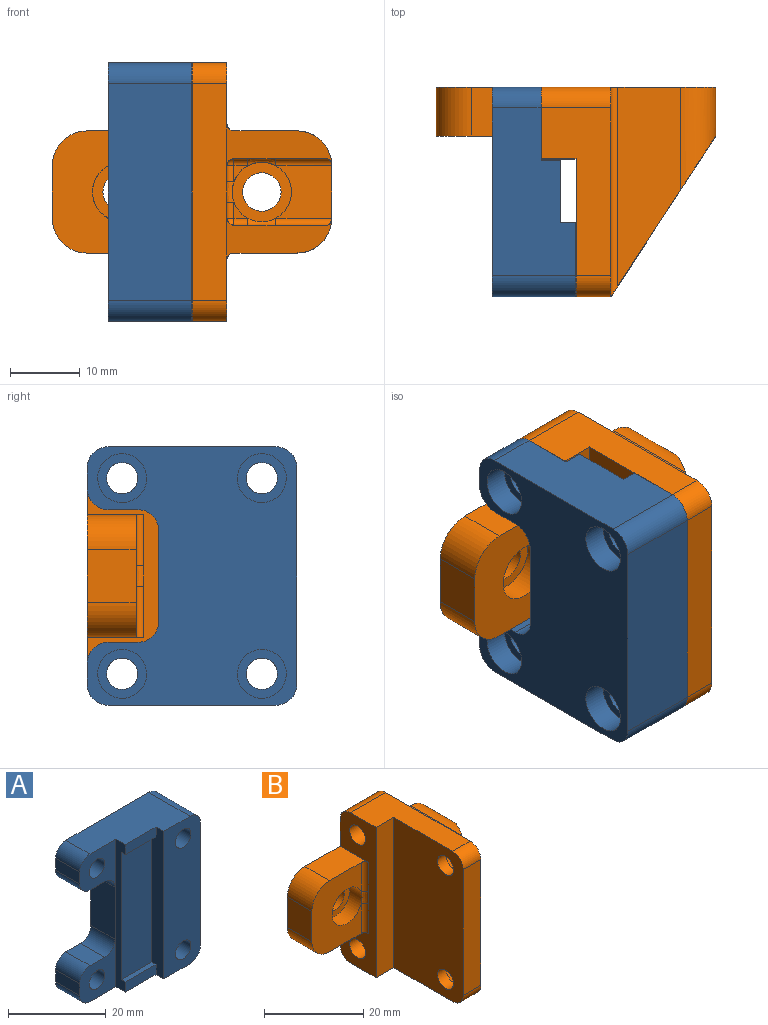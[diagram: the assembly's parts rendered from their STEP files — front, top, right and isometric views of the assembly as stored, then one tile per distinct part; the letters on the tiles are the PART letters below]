
ASSEMBLY  parts=2 mates=1
PART A: 38 faces, bbox 30x12x37 mm
  f0: cylinder r=2.25mm len=4.5mm, axis (0,1,0), area 49.5mm2, adj f6,f31
  f1: cylinder r=2.25mm len=4.5mm, axis (0,1,0), area 49.5mm2, adj f6,f33
  f2: cylinder r=2.25mm len=8.5mm, axis (0,1,0), area 120.2mm2, adj f16,f35
  f3: cylinder r=2.25mm len=8.5mm, axis (0,1,0), area 120.2mm2, adj f16,f37
  f4: plane 37x3.5mm, normal (-1,0,0), area 123.2mm2, adj f5,f8,f14,f16,f18,f19,f20,f21
  f5: plane 32x8.88mm, normal (0,-1,0), area 284mm2, adj f4,f17,f18,f20
  f6: plane 37x10.5mm, normal (0,-1,0), area 158.1mm2, adj f0,f1,f8,f9,f10,f11,f12,f13
  f7: plane 31x12mm, normal (1,0,0), area 372mm2, adj f15,f16,f22,f23
  f8: plane 24x12mm, normal (0,0,1), area 230.5mm2, adj f4,f6,f15,f16,f17,f19,f22,f24
  f9: plane 7x3mm, normal (-1,0,0), area 21mm2, adj f6,f15,f24,f25
  f10: plane 7x4.25mm, normal (0,0,-1), area 29.8mm2, adj f6,f15,f25,f26
  f11: plane 13x7mm, normal (-1,0,0), area 91mm2, adj f6,f15,f26,f27
  f12: plane 7x4.25mm, normal (0,0,1), area 29.8mm2, adj f6,f15,f27,f28
  f13: plane 7x3mm, normal (-1,0,0), area 21mm2, adj f6,f15,f28,f29
  f14: plane 24x12mm, normal (0,0,-1), area 230.5mm2, adj f4,f6,f15,f16,f17,f21,f23,f29
  f15: plane 37x30mm, normal (0,1,0), area 753.6mm2, adj f7,f8,f9,f10,f11,f12,f13,f14
  f16: plane 37x10.63mm, normal (0,-1,0), area 357.5mm2, adj f2,f3,f4,f7,f8,f14,f22,f23
  f17: plane 37x2.75mm, normal (-1,0,0), area 61.7mm2, adj f5,f6,f8,f14,f18,f19,f20,f21
  f18: plane 8.88x1.25mm, normal (0,0,-1), area 11.1mm2, adj f4,f5,f17,f19
  f19: plane 8.88x2.5mm, normal (0,-1,0), area 22.2mm2, adj f4,f8,f17,f18
  f20: plane 8.88x1.25mm, normal (0,0,1), area 11.1mm2, adj f4,f5,f17,f21
  f21: plane 8.88x2.5mm, normal (0,-1,0), area 22.2mm2, adj f4,f14,f17,f20
  f22: cylinder r=3mm len=12mm, axis (0,-1,0), area 56.5mm2, adj f7,f8,f15,f16
  f23: cylinder r=3mm len=12mm, axis (0,1,0), area 56.5mm2, adj f7,f14,f15,f16
  f24: cylinder r=3mm len=7mm, axis (0,1,0), area 33mm2, adj f6,f8,f9,f15
  f25: cylinder r=3mm len=7mm, axis (0,1,0), area 33mm2, adj f6,f9,f10,f15
  f26: cylinder r=3mm len=7mm, axis (0,-1,0), area 33mm2, adj f6,f10,f11,f15
  f27: cylinder r=3mm len=7mm, axis (0,1,0), area 33mm2, adj f6,f11,f12,f15
  f28: cylinder r=3mm len=7mm, axis (0,1,0), area 33mm2, adj f6,f12,f13,f15
  f29: cylinder r=3mm len=7mm, axis (0,1,0), area 33mm2, adj f6,f13,f14,f15
  f30: cylinder r=3.5mm len=7mm, axis (0,1,0), area 77mm2, adj f15,f31
  f31: plane 7x7mm, normal (0,1,0), area 22.6mm2, adj f0,f30
  f32: cylinder r=3.5mm len=7mm, axis (0,1,0), area 77mm2, adj f15,f33
  f33: plane 7x7mm, normal (0,1,0), area 22.6mm2, adj f1,f32
  f34: cylinder r=3.5mm len=7mm, axis (0,1,0), area 77mm2, adj f15,f35
  f35: plane 7x7mm, normal (0,1,0), area 22.6mm2, adj f2,f34
  f36: cylinder r=3.5mm len=7mm, axis (0,1,0), area 77mm2, adj f15,f37
  f37: plane 7x7mm, normal (0,1,0), area 22.6mm2, adj f3,f36
PART B: 88 faces, bbox 40.6x30.6x37.6 mm
  f0: cylinder r=2.25mm len=4.5mm, axis (-1,0,0), area 35.3mm2, adj f28,f81
  f1: cylinder r=2.25mm len=4.5mm, axis (-1,0,0), area 35.3mm2, adj f28,f74
  f2: cylinder r=2.25mm len=7.5mm, axis (-1,0,0), area 106mm2, adj f9,f67
  f3: cylinder r=2.25mm len=7.5mm, axis (-1,0,0), area 106mm2, adj f9,f60
  f4: plane 8x7.5mm, normal (0,-1,0), area 48mm2, adj f16,f24,f40,f52
  f5: plane 2.31x2mm, normal (0,-1,0), area 1.7mm2, adj f24,f47,f50
  f6: plane 30x8.75mm, normal (1,0,0), area 173.8mm2, adj f11,f18,f23,f39,f56,f59,f61,f62
  f7: plane 2.31x2mm, normal (0,-1,0), area 1.7mm2, adj f24,f42,f45
  f8: plane 22.03x7.5mm, normal (1,0,0), area 165mm2, adj f11,f43,f45,f46,f47,f48
  f9: plane 37x10.25mm, normal (-1,0,0), area 203.6mm2, adj f2,f3,f10,f18,f19,f21,f23,f29
  f10: plane 24x10mm, normal (0,0,-1), area 156.2mm2, adj f9,f22,f28,f29,f38,f58
  f11: plane 31x5mm, normal (0,-1,0), area 155mm2, adj f6,f8,f22,f28,f30,f32,f38,f39
  f12: plane 17.5x14mm, normal (0,-1,0), area 178mm2, adj f19,f20,f21,f26,f36,f37,f53,f55
  f13: cylinder r=2.75mm len=5.5mm, axis (0,1,0), area 60.5mm2, adj f23,f27
  f14: cylinder r=2.75mm len=5.5mm, axis (0,1,0), area 60.5mm2, adj f23,f25
  f15: plane 28.47x9mm, normal (0,0,-1), area 194.1mm2, adj f23,f30,f34,f57
  f16: plane 7.5x7mm, normal (1,0,0), area 52.5mm2, adj f4,f23,f34,f35
  f17: plane 28.47x9mm, normal (0,0,1), area 194.1mm2, adj f23,f32,f35,f56
  f18: plane 24x10mm, normal (0,0,1), area 156.2mm2, adj f6,f9,f28,f29,f39,f59
  f19: plane 10x8mm, normal (0,0,1), area 70.2mm2, adj f9,f12,f23,f36,f53
  f20: plane 7.5x7mm, normal (-1,0,0), area 52.5mm2, adj f12,f23,f36,f37
  f21: plane 10x8mm, normal (0,0,-1), area 70.2mm2, adj f9,f12,f23,f37,f55
  f22: plane 30x8.75mm, normal (1,0,0), area 173.8mm2, adj f10,f11,f23,f38,f57,f58,f68,f69
  f23: plane 40x31mm, normal (0,1,0), area 766.5mm2, adj f6,f9,f13,f14,f15,f16,f17,f19
  f24: cylinder r=4.25mm len=8.5mm, axis (0,-1,0), area 93.5mm2, adj f4,f5,f7,f25,f41,f46,f51
  f25: plane 8.5x8.5mm, normal (0,-1,0), area 33mm2, adj f14,f24
  f26: cylinder r=4.25mm len=8.5mm, axis (0,-1,0), area 93.5mm2, adj f12,f27,f54
  f27: plane 8.5x8.5mm, normal (0,-1,0), area 33mm2, adj f13,f26
  f28: plane 37x19.75mm, normal (-1,0,0), area 695.1mm2, adj f0,f1,f10,f11,f18,f29,f38,f39
  f29: plane 37x5mm, normal (0,-1,0), area 185mm2, adj f9,f10,f18,f28
  f30: plane 23.64x15.64mm, normal (0.84,-0.55,0), area 101.1mm2, adj f11,f15,f31,f34,f40,f43,f57
  f31: plane 20.6x13.35mm, normal (0,0,1), area 136.9mm2, adj f30,f40,f41,f42,f43
  f32: plane 23.64x15.64mm, normal (0.84,-0.55,0), area 101.1mm2, adj f11,f17,f33,f35,f48,f52,f56
  f33: plane 20.6x13.35mm, normal (0,0,-1), area 136.9mm2, adj f32,f48,f50,f51,f52
  f34: cylinder r=5mm len=14.67mm, axis (0,1,0), area 76.9mm2, adj f15,f16,f23,f30
  f35: cylinder r=5mm len=14.67mm, axis (0,-1,0), area 76.9mm2, adj f16,f17,f23,f32
  f36: cylinder r=5mm len=7mm, axis (0,1,0), area 55mm2, adj f12,f19,f20,f23
  f37: cylinder r=5mm len=7mm, axis (0,-1,0), area 55mm2, adj f12,f20,f21,f23
  f38: cylinder r=3mm len=5mm, axis (-1,0,0), area 23.6mm2, adj f10,f11,f22,f28
  f39: cylinder r=3mm len=5mm, axis (1,0,0), area 23.6mm2, adj f6,f11,f18,f28
  f40: cylinder r=1mm len=8mm, axis (-1,0,0), area 12.1mm2, adj f4,f30,f31,f41
  f41: bspline ~4.92x1.23mm, area 4.9mm2, adj f24,f31,f40,f42
  f42: cylinder r=1mm len=2mm, axis (-1,0,0), area 3.1mm2, adj f7,f31,f41,f44
  f43: cylinder r=1mm len=22mm, axis (0,1,0), area 33.4mm2, adj f8,f30,f31,f44
  f44: sphere r=1mm, area 1.6mm2, adj f42,f43,f45
  f45: cylinder r=1mm len=2.31mm, axis (0,0,1), area 3.6mm2, adj f7,f8,f44,f46
  f46: bspline ~3.99x1.27mm, area 4mm2, adj f8,f24,f45,f47
  f47: cylinder r=1mm len=2.31mm, axis (0,0,1), area 3.6mm2, adj f5,f8,f46,f49
  f48: cylinder r=1mm len=22mm, axis (0,1,0), area 33.4mm2, adj f8,f32,f33,f49
  f49: sphere r=1mm, area 1.6mm2, adj f47,f48,f50
  f50: cylinder r=1mm len=2mm, axis (-1,0,0), area 3.1mm2, adj f5,f33,f49,f51
  f51: bspline ~4x1mm, area 4.9mm2, adj f24,f33,f50,f52
  f52: cylinder r=1mm len=8mm, axis (-1,0,0), area 12.1mm2, adj f4,f32,f33,f51
  f53: cylinder r=1mm len=7.31mm, axis (0,0,-1), area 11.5mm2, adj f9,f12,f19,f54
  f54: bspline ~3.99x1.27mm, area 4mm2, adj f9,f26,f53,f55
  f55: cylinder r=1mm len=7.31mm, axis (0,0,-1), area 11.5mm2, adj f9,f12,f21,f54
  f56: cylinder r=1mm len=30mm, axis (0,-1,0), area 45.9mm2, adj f6,f17,f23,f32
  f57: cylinder r=1mm len=30mm, axis (0,1,0), area 45.9mm2, adj f15,f22,f23,f30
  f58: cylinder r=3mm len=10mm, axis (1,0,0), area 47.1mm2, adj f9,f10,f22,f23
  f59: cylinder r=3mm len=10mm, axis (-1,0,0), area 47.1mm2, adj f6,f9,f18,f23
  f60: plane 8.08x7mm, normal (1,0,0), area 26.5mm2, adj f3,f61,f62,f63,f64,f65,f66
  f61: plane 4.04x2.5mm, normal (0,0,-1), area 10.1mm2, adj f6,f60,f62,f66
  f62: plane 3.5x2.5mm, normal (0,0.87,-0.5), area 10.1mm2, adj f6,f60,f61,f63
  f63: plane 3.5x2.5mm, normal (0,0.87,0.5), area 10.1mm2, adj f6,f60,f62,f64
  f64: plane 4.04x2.5mm, normal (0,0,1), area 10.1mm2, adj f6,f60,f63,f65
  f65: plane 3.5x2.5mm, normal (0,-0.87,0.5), area 10.1mm2, adj f6,f60,f64,f66
  f66: plane 3.5x2.5mm, normal (0,-0.87,-0.5), area 10.1mm2, adj f6,f60,f61,f65
  f67: plane 8.08x7mm, normal (1,0,0), area 26.5mm2, adj f2,f68,f69,f70,f71,f72,f73
  f68: plane 4.04x2.5mm, normal (0,0,1), area 10.1mm2, adj f22,f67,f69,f73
  f69: plane 3.5x2.5mm, normal (0,-0.87,0.5), area 10.1mm2, adj f22,f67,f68,f70
  f70: plane 3.5x2.5mm, normal (0,-0.87,-0.5), area 10.1mm2, adj f22,f67,f69,f71
  f71: plane 4.04x2.5mm, normal (0,0,-1), area 10.1mm2, adj f22,f67,f70,f72
  f72: plane 3.5x2.5mm, normal (0,0.87,-0.5), area 10.1mm2, adj f22,f67,f71,f73
  f73: plane 3.5x2.5mm, normal (0,0.87,0.5), area 10.1mm2, adj f22,f67,f68,f72
  f74: plane 8.08x7mm, normal (1,0,0), area 26.5mm2, adj f1,f75,f76,f77,f78,f79,f80
  f75: plane 4.04x2.5mm, normal (0,0,-1), area 10.1mm2, adj f22,f74,f76,f80
  f76: plane 3.5x2.5mm, normal (0,0.87,-0.5), area 10.1mm2, adj f22,f74,f75,f77
  f77: plane 3.5x2.5mm, normal (0,0.87,0.5), area 10.1mm2, adj f22,f74,f76,f78
  f78: plane 4.04x2.5mm, normal (0,0,1), area 10.1mm2, adj f22,f74,f77,f79
  f79: plane 3.5x2.5mm, normal (0,-0.87,0.5), area 10.1mm2, adj f22,f74,f78,f80
  f80: plane 3.5x2.5mm, normal (0,-0.87,-0.5), area 10.1mm2, adj f22,f74,f75,f79
  f81: plane 8.08x7mm, normal (1,0,0), area 26.5mm2, adj f0,f82,f83,f84,f85,f86,f87
  f82: plane 4.04x2.5mm, normal (0,0,-1), area 10.1mm2, adj f6,f81,f83,f87
  f83: plane 3.5x2.5mm, normal (0,0.87,-0.5), area 10.1mm2, adj f6,f81,f82,f84
  f84: plane 3.5x2.5mm, normal (0,0.87,0.5), area 10.1mm2, adj f6,f81,f83,f85
  f85: plane 4.04x2.5mm, normal (0,0,1), area 10.1mm2, adj f6,f81,f84,f86
  f86: plane 3.5x2.5mm, normal (0,-0.87,0.5), area 10.1mm2, adj f6,f81,f85,f87
  f87: plane 3.5x2.5mm, normal (0,-0.87,-0.5), area 10.1mm2, adj f6,f81,f82,f86
PLACE A rot(axis=(0.71,-0.71,0),180deg) t=(-12,-20.12,0)mm
PLACE B at identity
MATE fastened B.f3 <-> A.f1  axis (-1,0,0) through (-5,-5,14)mm
